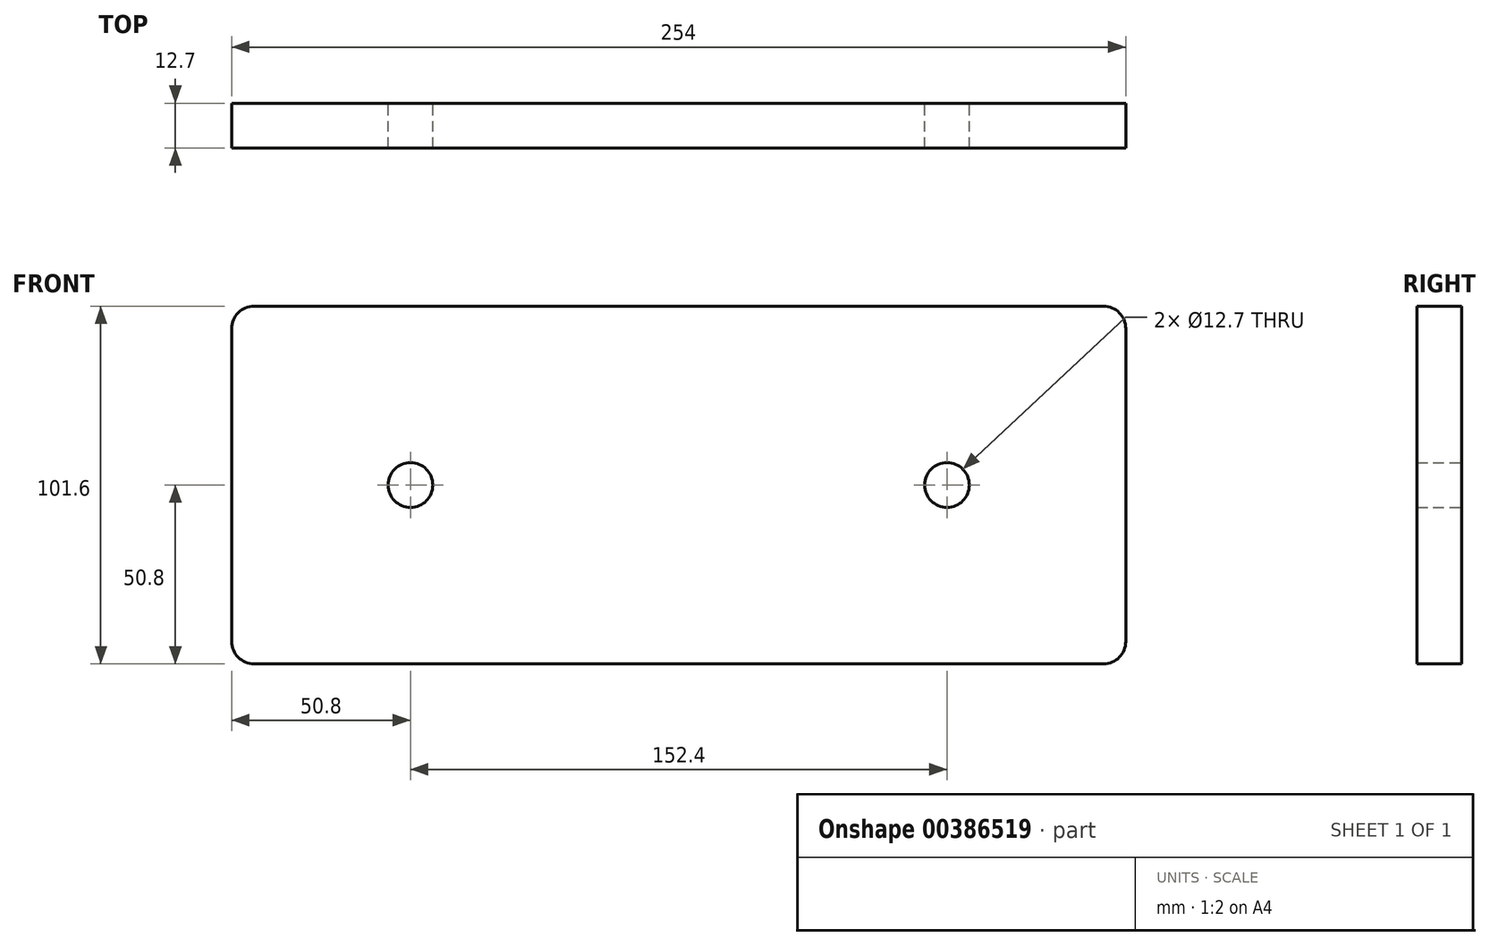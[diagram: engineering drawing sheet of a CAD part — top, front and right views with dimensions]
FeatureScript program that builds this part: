
annotation { "Feature Type Name" : "Feature", "Feature Type Description" : "" }
export const myFeature = defineFeature(function(context is Context, id is Id, definition is map)
    precondition{}
    {
        {
            var Q0;
            Q0=qCreatedBy(makeId("Front.planeOp"),FACE);
            var sketch = newSketch(context, id + "F0", { "sketchPlane" : qUnion([Q0])});
            skLineSegment(sketch, "E0.bottom", {"start": v(6.35, 0) * mm, "end": v(247.65, 0) * mm});
            skLineSegment(sketch, "E0.top", {"start": v(6.35, 101.6) * mm, "end": v(247.65, 101.6) * mm});
            skLineSegment(sketch, "E0.left", {"start": v(0, 6.35) * mm, "end": v(0, 95.25) * mm});
            skLineSegment(sketch, "E0.right", {"start": v(254, 6.35) * mm, "end": v(254, 95.25) * mm});
            skPoint(sketch, "E1.visualSharp", {"position": v(0, 101.6) * mm});
            skArc(sketch, "E1.filletArc", {"start": v(6.35, 101.6) * mm, "mid": v(1.86, 99.74) * mm, "end": v(0, 95.25) * mm});
            skPoint(sketch, "E2.visualSharp", {"position": v(254, 101.6) * mm});
            skArc(sketch, "E2.filletArc", {"start": v(254, 95.25) * mm, "mid": v(252.14, 99.74) * mm, "end": v(247.65, 101.6) * mm});
            skPoint(sketch, "E3.visualSharp", {"position": v(254, 0) * mm});
            skArc(sketch, "E3.filletArc", {"start": v(247.65, 0) * mm, "mid": v(252.14, 1.86) * mm, "end": v(254, 6.35) * mm});
            skPoint(sketch, "E4.visualSharp", {"position": v(0, 0) * mm});
            skArc(sketch, "E4.filletArc", {"start": v(0, 6.35) * mm, "mid": v(1.86, 1.86) * mm, "end": v(6.35, 0) * mm});
            skPoint(sketch, "E5", {"position": v(50.8, 50.8) * mm});
            skPoint(sketch, "E6", {"position": v(203.2, 50.8) * mm});
            skSolve(sketch);
        }
        {
            var Q0;
            Q0 = qSketchRegion(id + "F0", true);
            extrude(context, id + "F1", {"entities" : qUnion([Q0]), "depth" : 12.7 * mm});
        }
        {
            var Q0;
            Q0=sQuery(id+"F0.wireOp",VERTEX,"E5");
            var Q1;
            Q1=sQuery(id+"F0.wireOp",VERTEX,"E6");
            var Q2;
            Q2=makeQuery(id+"F1.opExtrude","SWEPT_BODY",BODY,{"disambiguationData":[OSD([sQuery(id+"F0.wireOp",EDGE,"E0.bottom"),sQuery(id+"F0.wireOp",EDGE,"E0.top"),sQuery(id+"F0.wireOp",EDGE,"E0.left"),sQuery(id+"F0.wireOp",EDGE,"E0.right"),sQuery(id+"F0.wireOp",EDGE,"E1.filletArc"),sQuery(id+"F0.wireOp",EDGE,"E2.filletArc"),sQuery(id+"F0.wireOp",EDGE,"E3.filletArc"),sQuery(id+"F0.wireOp",EDGE,"E4.filletArc")])]});
            hole(context, id + "F2", {"style" : HoleStyle.SIMPLE, "endStyle" : HoleEndStyle.THROUGH, "oppositeDirection" : true, "holeDiameter" : 12.7 * mm, "isTappedThrough" : true, "tappedDepth" : 12.7 * mm, "tapClearance" : 3, "locations" : qUnion([Q0, Q1]), "scope" : qUnion([Q2])});
        }
    });
